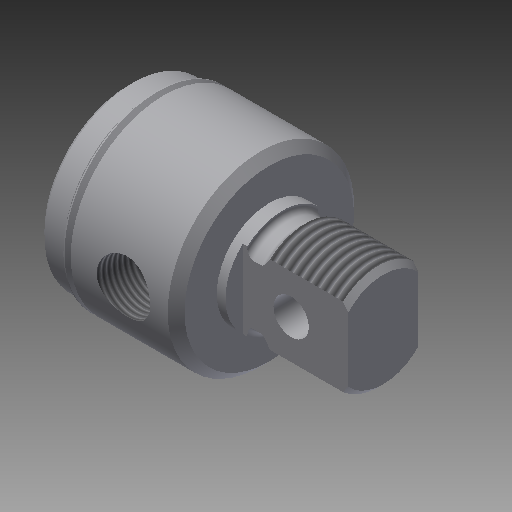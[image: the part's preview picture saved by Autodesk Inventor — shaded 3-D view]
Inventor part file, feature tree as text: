
AUTODESK INVENTOR PART (.ipt)
format: ipt  version: 2019 (Build 230136000, 136)  size: 341,504 bytes
history: native  units: in
note: dims shown in document units (in); Inventor stores cm internally (conversion verified against a paired STEP export)
features: other x154, sketch x8, revolve x5, thread x2, extrude x2, hole x1
ambient origin geometry x8: Origin, YZ Plane, XZ Plane, XY Plane, X Axis, Y Axis, Z Axis, Center Point
bodies: Solid1 (feature_tree)
feature tree (172):
  revolve  "Revolution1"  Angle=360.0deg
  revolve  "Revolution2"  [1 undecoded]
  thread  "Thread1"  [1 undecoded]
  extrude  "Extrusion1"  TaperAngle=360.0deg  [1 undecoded]
  hole  "Hole1"  [1 undecoded]
  revolve  "Revolution3"  [1 undecoded]
  thread  "Thread2"  [1 undecoded]
  revolve  "Revolution4"  [1 undecoded]
  revolve  "Revolution5"  [1 undecoded]
  extrude  "Extrusion2"  [1 undecoded]
  other  "1_XY"
  other  "1_YZ"
  other  "1_ZX"
  other  "1_X"
  other  "1_Y"
  other  "1_Z"
  other  "1_Center"
  other  "c1_XY"
  other  "c1_YZ"
  other  "c1_ZX"
  other  "c1_X"
  other  "c1_Y"
  other  "c1_Z"
  other  "c1_Center"
  other  "c2_XY"
  other  "c2_YZ"
  other  "c2_ZX"
  other  "c2_X"
  other  "c2_Y"
  other  "c2_Z"
  other  "c2_Center"
  other  "cc1_XY"
  other  "cc1_YZ"
  other  "cc1_ZX"
  other  "cc1_X"
  other  "cc1_Y"
  other  "cc1_Z"
  other  "cc1_Center"
  other  "cc2_XY"
  other  "cc2_YZ"
  other  "cc2_ZX"
  other  "cc2_X"
  other  "cc2_Y"
  other  "cc2_Z"
  other  "cc2_Center"
  other  "lovra1_XY"
  other  "lovra1_YZ"
  other  "lovra1_ZX"
  other  "lovra1_X"
  other  "lovra1_Y"
  other  "lovra1_Z"
  other  "lovra1_Center"
  other  "lovra2_XY"
  other  "lovra2_YZ"
  other  "lovra2_ZX"
  other  "lovra2_X"
  other  "lovra2_Y"
  other  "lovra2_Z"
  other  "lovra2_Center"
  other  "lovra21_XY"
  other  "lovra21_YZ"
  other  "lovra21_ZX"
  other  "lovra21_X"
  other  "lovra21_Y"
  other  "lovra21_Z"
  other  "lovra21_Center"
  other  "lovra22_XY"
  other  "lovra22_YZ"
  other  "lovra22_ZX"
  other  "lovra22_X"
  other  "lovra22_Y"
  other  "lovra22_Z"
  other  "lovra22_Center"
  other  "lovra3_XY"
  other  "lovra3_YZ"
  other  "lovra3_ZX"
  other  "lovra3_X"
  other  "lovra3_Y"
  other  "lovra3_Z"
  other  "lovra3_Center"
  other  "olen_XY"
  other  "olen_YZ"
  other  "olen_ZX"
  other  "olen_X"
  other  "olen_Y"
  other  "olen_Z"
  other  "olen_Center"
  other  "p1_XY"
  other  "p1_YZ"
  other  "p1_ZX"
  other  "p1_X"
  other  "p1_Y"
  other  "p1_Z"
  other  "p1_Center"
  other  "p2_XY"
  other  "p2_YZ"
  other  "p2_ZX"
  other  "p2_X"
  other  "p2_Y"
  other  "p2_Z"
  other  "p2_Center"
  other  "port_XY"
  other  "port_YZ"
  other  "port_ZX"
  other  "port_X"
  other  "port_Y"
  other  "port_Z"
  other  "port_Center"
  other  "port2_XY"
  other  "port2_YZ"
  other  "port2_ZX"
  other  "port2_X"
  other  "port2_Y"
  other  "port2_Z"
  other  "port2_Center"
  other  "thd1_XY"
  other  "thd1_YZ"
  other  "thd1_ZX"
  other  "thd1_X"
  other  "thd1_Y"
  other  "thd1_Z"
  other  "thd1_Center"
  other  "thd2_XY"
  other  "thd2_YZ"
  other  "thd2_ZX"
  other  "thd2_X"
  other  "thd2_Y"
  other  "thd2_Z"
  other  "thd2_Center"
  other  "to_mounting_bracket_XY"
  other  "to_mounting_bracket_YZ"
  other  "to_mounting_bracket_ZX"
  other  "to_mounting_bracket_X"
  other  "to_mounting_bracket_Y"
  other  "to_mounting_bracket_Z"
  other  "to_mounting_bracket_Center"
  other  "to_nut_XY"
  other  "to_nut_YZ"
  other  "to_nut_ZX"
  other  "to_nut_X"
  other  "to_nut_Y"
  other  "to_nut_Z"
  other  "to_nut_Center"
  other  "to_pin_XY"
  other  "to_pin_YZ"
  other  "to_pin_ZX"
  other  "to_pin_X"
  other  "to_pin_Y"
  other  "to_pin_Z"
  other  "to_pin_Center"
  other  "to_screw_XY"
  other  "to_screw_YZ"
  other  "to_screw_ZX"
  other  "to_screw_X"
  other  "to_screw_Y"
  other  "to_screw_Z"
  other  "to_screw_Center"
  other  "to_tube_XY"
  other  "to_tube_YZ"
  other  "to_tube_ZX"
  other  "to_tube_X"
  other  "to_tube_Y"
  other  "to_tube_Z"
  other  "to_tube_Center"
  sketch  "Sketch_18"  dims[d14=0.2731in d15=0.0in d16=360.0deg]
  sketch  "Sketch_15"  dims[d6=0.5in d7=0.75in d8=0.375in d9=0.25in d10=0.5635in d11=0.8932in d12=120.0deg d13=360.0deg]
  sketch  "Sketch_9"  dims[d2=0.5195in d3=0.0in d4=0.75in d5=0.0in]
  sketch  "Sketch4"  dims[d0=360.0deg d1=360.0deg]
  sketch  "Sketch_68"
  sketch  "Sketch_20"  dims[d17=360.0deg d18=0.75in d19=0.0in]
  sketch  "Sketch_24"  dims[d20=0.0in d21=0.0in d22=0.0in d23=0.0in d24=0.0in d25=0.0in d26=0.0in d27=0.0in]
  sketch  "Sketch_43"
note: 9 required parameter values undecoded (feature->parameter linkage not recoverable at this tier; creation-order binding heuristic only, values carry confidence <= 0.55)